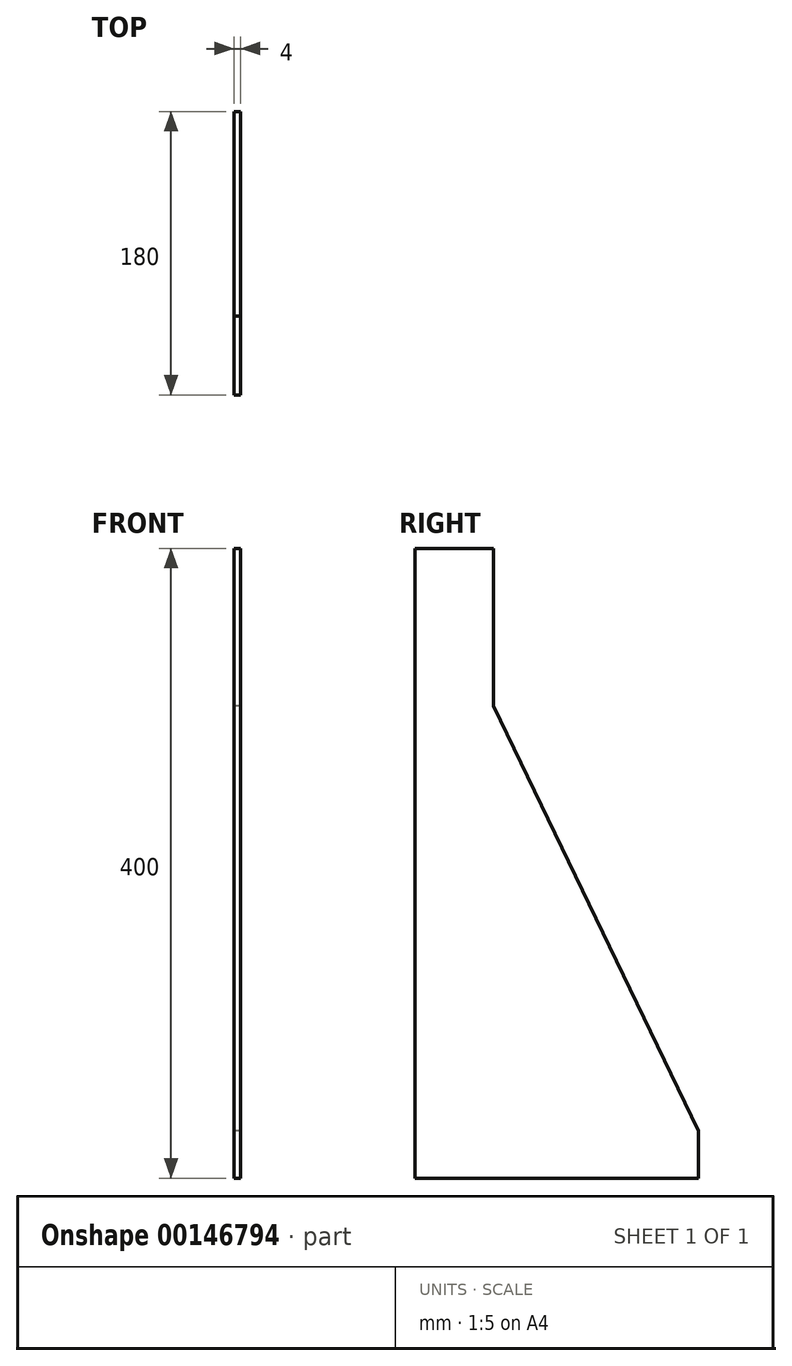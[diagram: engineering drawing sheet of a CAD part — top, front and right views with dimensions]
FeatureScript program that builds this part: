
annotation { "Feature Type Name" : "Feature", "Feature Type Description" : "" }
export const myFeature = defineFeature(function(context is Context, id is Id, definition is map)
    precondition{}
    {
        {
            var Q0;
            Q0=qCreatedBy(makeId("Right.planeOp"),FACE);
            var sketch = newSketch(context, id + "F0", { "sketchPlane" : qUnion([Q0])});
            skLineSegment(sketch, "E0", {"start": v(0, 400) * mm, "end": v(0, 0) * mm});
            skLineSegment(sketch, "E1", {"start": v(0, 0) * mm, "end": v(180, 0) * mm});
            skLineSegment(sketch, "E2", {"start": v(180, 30) * mm, "end": v(50, 300) * mm});
            skLineSegment(sketch, "E3", {"start": v(50, 300) * mm, "end": v(50, 400) * mm});
            skLineSegment(sketch, "E4", {"start": v(50, 400) * mm, "end": v(0, 400) * mm});
            skLineSegment(sketch, "E5", {"start": v(180, 0) * mm, "end": v(180, 30) * mm});
            skSolve(sketch);
        }
        {
            var Q0;
            Q0 = qSketchRegion(id + "F0", true);
            extrude(context, id + "F1", {"entities" : qUnion([Q0]), "depth" : 4 * mm});
        }
    });
